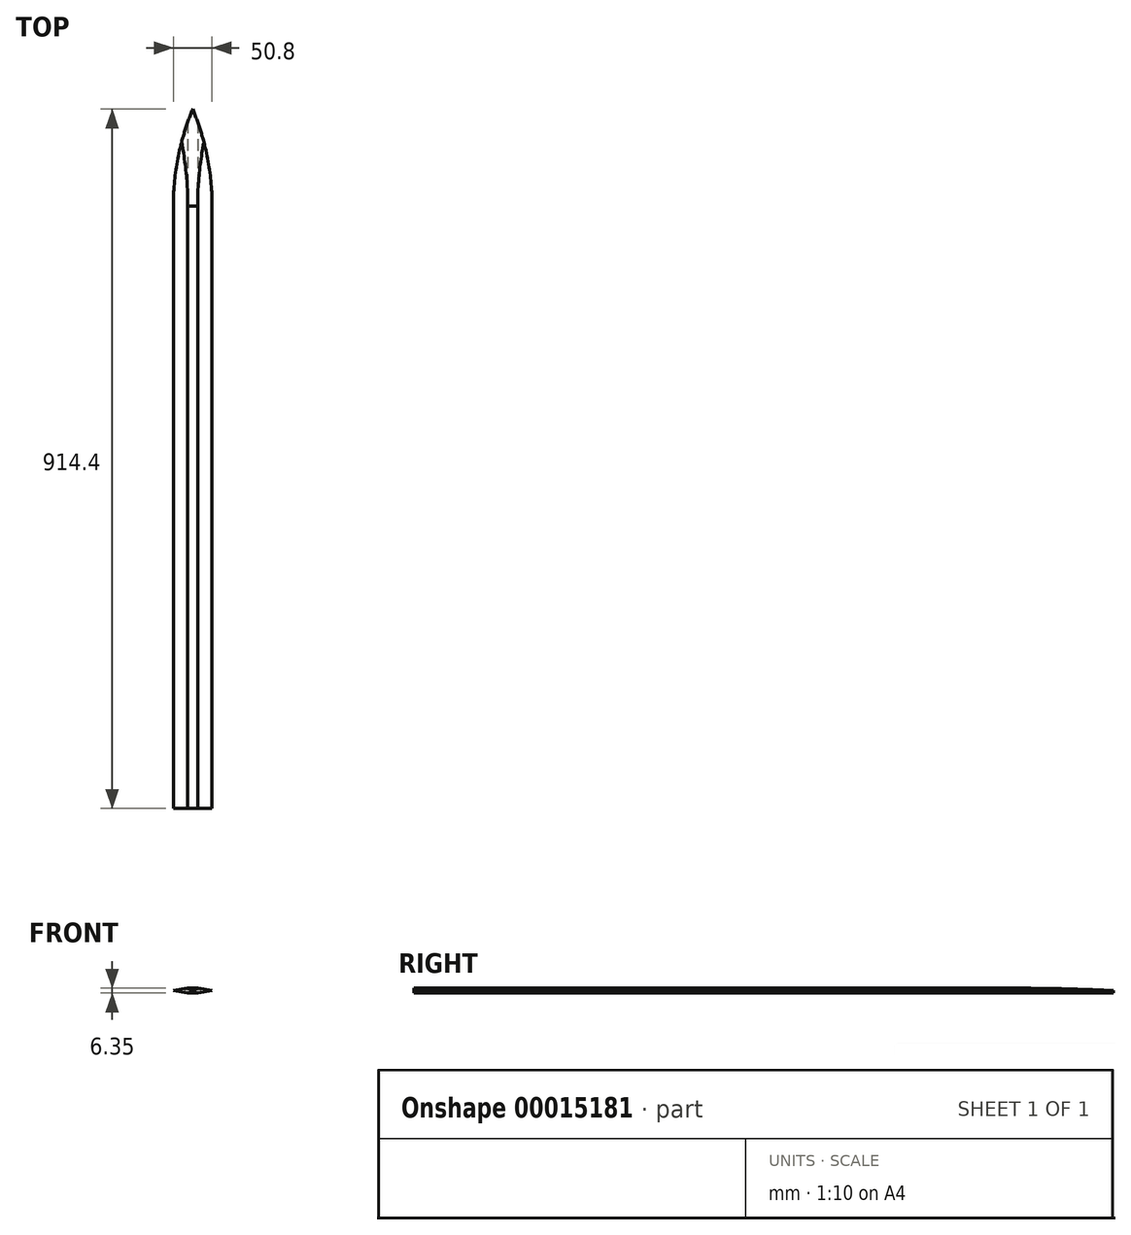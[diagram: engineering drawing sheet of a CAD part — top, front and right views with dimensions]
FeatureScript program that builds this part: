
annotation { "Feature Type Name" : "Feature", "Feature Type Description" : "" }
export const myFeature = defineFeature(function(context is Context, id is Id, definition is map)
    precondition{}
    {
        {
            var Q0;
            Q0=qCreatedBy(makeId("Top.planeOp"),FACE);
            var sketch = newSketch(context, id + "F0", { "sketchPlane" : qUnion([Q0])});
            skLineSegment(sketch, "E0.bottom", {"start": v(-196.6, 454.87) * mm, "end": v(-145.8, 454.87) * mm});
            skLineSegment(sketch, "E0.top", {"start": v(-196.6, -459.53) * mm, "end": v(-145.8, -459.53) * mm});
            skLineSegment(sketch, "E0.left", {"start": v(-196.6, 454.87) * mm, "end": v(-196.6, -459.53) * mm});
            skLineSegment(sketch, "E0.right", {"start": v(-145.8, 454.87) * mm, "end": v(-145.8, -459.53) * mm});
            skSolve(sketch);
        }
        {
            var Q0;
            Q0=makeQuery(id+"F0.imprint","IMPRINT",FACE,{"disambiguationData":[TD([[makeQuery(id+"F0.imprint","IMPRINT",EDGE,{"derivedFrom":sQuery(id+"F0.wireOp",EDGE,"E0.bottom")}),-1.0]])]});
            extrude(context, id + "F1", {"entities" : qUnion([Q0]), "depth" : 6.35 * mm});
        }
        {
            var Q0;
            Q0=makeQuery(id+"F1.opExtrude","SWEPT_FACE",FACE,{"disambiguationData":[OSD([sQuery(id+"F0.wireOp",EDGE,"E0.top")])]});
            var sketch = newSketch(context, id + "F2", { "sketchPlane" : qUnion([Q0])});
            skLineSegment(sketch, "E1", {"start": v(-171.2, 6.35) * mm, "end": v(-171.2, 0) * mm, "construction": true});
            skLineSegment(sketch, "E2", {"start": v(-196.6, 3.18) * mm, "end": v(-145.8, 3.18) * mm, "construction": true});
            skLineSegment(sketch, "E3", {"start": v(-177.56, 6.35) * mm, "end": v(-177.56, 3.17) * mm, "construction": true});
            skLineSegment(sketch, "E4", {"start": v(-164.86, 6.35) * mm, "end": v(-164.86, 3.17) * mm, "construction": true});
            skLineSegment(sketch, "E5", {"start": v(-177.56, 3.17) * mm, "end": v(-177.56, 0) * mm, "construction": true});
            skLineSegment(sketch, "E6", {"start": v(-164.86, 3.17) * mm, "end": v(-164.86, 0) * mm, "construction": true});
            skLineSegment(sketch, "E7", {"start": v(-177.56, 4.76) * mm, "end": v(-164.86, 4.76) * mm, "construction": true});
            skLineSegment(sketch, "E8", {"start": v(-177.56, 1.59) * mm, "end": v(-164.86, 1.59) * mm, "construction": true});
            skArc(sketch, "E9", {"start": v(-177.56, 6.35) * mm, "mid": v(-171.2, 4.76) * mm, "end": v(-164.86, 6.35) * mm});
            skArc(sketch, "E10", {"start": v(-164.86, 0) * mm, "mid": v(-171.2, 1.59) * mm, "end": v(-177.56, 0) * mm});
            skLineSegment(sketch, "E11", {"start": v(-145.8, 3.18) * mm, "end": v(-164.86, 0) * mm});
            skLineSegment(sketch, "E12", {"start": v(-145.8, 3.18) * mm, "end": v(-164.86, 6.35) * mm});
            skLineSegment(sketch, "E13", {"start": v(-177.56, 6.35) * mm, "end": v(-196.6, 3.18) * mm});
            skLineSegment(sketch, "E14", {"start": v(-196.6, 3.18) * mm, "end": v(-177.56, 0) * mm});
            skSolve(sketch);
        }
        {
            var Q0;
            {var subQ2=sQuery(id+"F2.wireOp",EDGE,"E13");Q0=makeQuery(id+"F2.imprint","IMPRINT",FACE,{"disambiguationData":[TD([[makeQuery(id+"F2.imprint","IMPRINT",EDGE,{"derivedFrom":subQ2}),-1.0]])]});}
            var Q1;
            {var subQ2=sQuery(id+"F2.wireOp",EDGE,"E14");Q1=makeQuery(id+"F2.imprint","IMPRINT",FACE,{"disambiguationData":[TD([[makeQuery(id+"F2.imprint","IMPRINT",EDGE,{"derivedFrom":subQ2}),-1.0]])]});}
            var Q2;
            {var subQ1=sQuery(id+"F2.wireOp",EDGE,"E10");Q2=makeQuery(id+"F2.imprint","IMPRINT",FACE,{"disambiguationData":[TD([[makeQuery(id+"F2.imprint","IMPRINT",EDGE,{"derivedFrom":subQ1}),1.0]])]});}
            var Q3;
            {var subQ1=sQuery(id+"F2.wireOp",EDGE,"E9");Q3=makeQuery(id+"F2.imprint","IMPRINT",FACE,{"disambiguationData":[TD([[makeQuery(id+"F2.imprint","IMPRINT",EDGE,{"derivedFrom":subQ1}),1.0]])]});}
            var Q4;
            {var subQ2=sQuery(id+"F2.wireOp",EDGE,"E12");Q4=makeQuery(id+"F2.imprint","IMPRINT",FACE,{"disambiguationData":[TD([[makeQuery(id+"F2.imprint","IMPRINT",EDGE,{"derivedFrom":subQ2}),-1.0]])]});}
            var Q5;
            {var subQ2=sQuery(id+"F2.wireOp",EDGE,"E11");Q5=makeQuery(id+"F2.imprint","IMPRINT",FACE,{"disambiguationData":[TD([[makeQuery(id+"F2.imprint","IMPRINT",EDGE,{"derivedFrom":subQ2}),1.0]])]});}
            extrude(context, id + "F3", {"entities" : qUnion([Q0, Q1, Q2, Q3, Q4, Q5]), "operationType" : NewBodyOperationType.REMOVE, "oppositeDirection" : true, "depth" : 787.4 * mm});
        }
        {
            var Q0;
            Q0=makeQuery(id+"F1.opExtrude","CAP_FACE",FACE,{"disambiguationData":[OSD([sQuery(id+"F0.wireOp",EDGE,"E0.bottom"),sQuery(id+"F0.wireOp",EDGE,"E0.top"),sQuery(id+"F0.wireOp",EDGE,"E0.left"),sQuery(id+"F0.wireOp",EDGE,"E0.right")])],"isStart":true});
            var sketch = newSketch(context, id + "F4", { "sketchPlane" : qUnion([Q0])});
            skArc(sketch, "E15", {"start": v(-171.2, -454.87) * mm, "mid": v(-152.22, -392.62) * mm, "end": v(-145.8, -327.87) * mm});
            skArc(sketch, "E16", {"start": v(-196.6, -327.87) * mm, "mid": v(-190.2, -392.62) * mm, "end": v(-171.2, -454.87) * mm});
            skSolve(sketch);
        }
        {
            var Q0;
            Q0=makeQuery(id+"F1.opExtrude","SWEPT_FACE",FACE,{"disambiguationData":[OSD([sQuery(id+"F0.wireOp",EDGE,"E0.left")])]});
            var sketch = newSketch(context, id + "F5", { "sketchPlane" : qUnion([Q0])});
            skArc(sketch, "E17", {"start": v(-327.87, 6.35) * mm, "mid": v(-391.39, 5.56) * mm, "end": v(-454.87, 3.17) * mm});
            skArc(sketch, "E18", {"start": v(-454.87, 3.18) * mm, "mid": v(-391.39, 0.8) * mm, "end": v(-327.87, 0) * mm});
            skSolve(sketch);
        }
        {
            var Q0;
            Q0 = qSketchRegion(id + "F5", true);
            var Q1;
            {var subQ2=sQuery(id+"F5.wireOp",EDGE,"E17");Q1=makeQuery(id+"F5.imprint","IMPRINT",FACE,{"disambiguationData":[TD([[makeQuery(id+"F5.imprint","IMPRINT",EDGE,{"derivedFrom":subQ2}),-1.0]])]});}
            extrude(context, id + "F6", {"entities" : qUnion([Q0, Q1]), "operationType" : NewBodyOperationType.REMOVE, "oppositeDirection" : true, "depth" : 62.83 * mm});
        }
        {
            var Q0;
            {var subQ1=sQuery(id+"F4.wireOp",EDGE,"E15");Q0=makeQuery(id+"F4.imprint","IMPRINT",FACE,{"disambiguationData":[TD([[makeQuery(id+"F4.imprint","IMPRINT",EDGE,{"derivedFrom":subQ1}),-1.0]])]});}
            var Q1;
            {var subQ1=sQuery(id+"F4.wireOp",EDGE,"E16");Q1=makeQuery(id+"F4.imprint","IMPRINT",FACE,{"disambiguationData":[TD([[makeQuery(id+"F4.imprint","IMPRINT",EDGE,{"derivedFrom":subQ1}),-1.0]])]});}
            extrude(context, id + "F7", {"entities" : qUnion([Q0, Q1]), "operationType" : NewBodyOperationType.REMOVE, "oppositeDirection" : true, "depth" : 25.4 * mm});
        }
        {
            var Q0;
            Q0=makeQuery(id+"F3.boolean.opBoolean","COPY",FACE,{"derivedFrom":makeQuery(id+"F3.opExtrude","CAP_FACE",FACE,{"disambiguationData":[OSD([sQuery(id+"F0.wireOp",EDGE,"E0.top"),sQuery(id+"F0.wireOp",EDGE,"E0.right"),sQuery(id+"F2.wireOp",EDGE,"E11")])],"isStart":false})});
            var Q1;
            Q1=makeQuery(id+"F3.boolean.opBoolean","COPY",FACE,{"derivedFrom":makeQuery(id+"F3.opExtrude","CAP_FACE",FACE,{"disambiguationData":[OSD([sQuery(id+"F0.wireOp",EDGE,"E0.top"),sQuery(id+"F0.wireOp",EDGE,"E0.right"),sQuery(id+"F2.wireOp",EDGE,"E12")])],"isStart":false})});
            var Q2;
            Q2=makeQuery(id+"F3.boolean.opBoolean","COPY",FACE,{"derivedFrom":makeQuery(id+"F3.opExtrude","CAP_FACE",FACE,{"disambiguationData":[OSD([sQuery(id+"F0.wireOp",EDGE,"E0.top"),sQuery(id+"F0.wireOp",EDGE,"E0.left"),sQuery(id+"F2.wireOp",EDGE,"E14")])],"isStart":false})});
            var Q3;
            Q3=makeQuery(id+"F3.boolean.opBoolean","COPY",FACE,{"derivedFrom":makeQuery(id+"F3.opExtrude","CAP_FACE",FACE,{"disambiguationData":[OSD([sQuery(id+"F0.wireOp",EDGE,"E0.top"),sQuery(id+"F0.wireOp",EDGE,"E0.left"),sQuery(id+"F2.wireOp",EDGE,"E13")])],"isStart":false})});
            extrude(context, id + "F8", {"entities" : qUnion([Q0, Q1, Q2, Q3]), "operationType" : NewBodyOperationType.REMOVE, "oppositeDirection" : true, "depth" : 161.17 * mm});
        }
        {
            var Q0;
            Q0=makeQuery(id+"F1.opExtrude","SWEPT_FACE",FACE,{"disambiguationData":[OSD([sQuery(id+"F0.wireOp",EDGE,"E0.top")])]});
            var sketch = newSketch(context, id + "F9", { "sketchPlane" : qUnion([Q0])});
            skLineSegment(sketch, "E19.bottom", {"start": v(-177.56, 6.35) * mm, "end": v(-177.56, 6.35) * mm});
            skLineSegment(sketch, "E19.top", {"start": v(-177.56, 0) * mm, "end": v(-177.56, 0) * mm});
            skLineSegment(sketch, "E19.left", {"start": v(-177.56, 6.35) * mm, "end": v(-177.56, 0) * mm});
            skLineSegment(sketch, "E19.right", {"start": v(-177.56, 6.35) * mm, "end": v(-177.56, 0) * mm});
            skLineSegment(sketch, "E20.bottom", {"start": v(-164.86, 0) * mm, "end": v(-164.86, 0) * mm});
            skLineSegment(sketch, "E20.top", {"start": v(-164.86, 6.35) * mm, "end": v(-164.86, 6.35) * mm});
            skLineSegment(sketch, "E20.left", {"start": v(-164.86, 0) * mm, "end": v(-164.86, 6.35) * mm});
            skLineSegment(sketch, "E20.right", {"start": v(-164.86, 0) * mm, "end": v(-164.86, 6.35) * mm});
            skLineSegment(sketch, "E21", {"start": v(-177.56, 6.35) * mm, "end": v(-164.86, 6.35) * mm});
            skLineSegment(sketch, "E22", {"start": v(-164.86, 0) * mm, "end": v(-177.56, 0) * mm});
            skSolve(sketch);
        }
        {
            var Q0;
            Q0=makeQuery(id+"F9.imprint","IMPRINT",FACE,{"disambiguationData":[TD([[makeQuery(id+"F9.imprint","IMPRINT",EDGE,{"derivedFrom":sQuery(id+"F9.wireOp",EDGE,"E22")}),-1.0]])]});
            var Q1;
            Q1=makeQuery(id+"F9.imprint","IMPRINT",FACE,{"disambiguationData":[TD([[makeQuery(id+"F9.imprint","IMPRINT",EDGE,{"derivedFrom":sQuery(id+"F9.wireOp",EDGE,"E19.right")}),1.0]])]});
            var Q2;
            Q2=makeQuery(id+"F9.imprint","IMPRINT",FACE,{"disambiguationData":[TD([[makeQuery(id+"F9.imprint","IMPRINT",EDGE,{"derivedFrom":sQuery(id+"F9.wireOp",EDGE,"E21")}),-1.0]])]});
            extrude(context, id + "F10", {"entities" : qUnion([Q0, Q1, Q2]), "operationType" : NewBodyOperationType.ADD, "depth" : 127 * mm});
        }
        {
            var Q0;
            Q0=makeQuery(id+"F10.opExtrude","SWEPT_FACE",FACE,{"disambiguationData":[OSD([sQuery(id+"F9.wireOp",EDGE,"E21")])]});
            extrude(context, id + "F11", {"entities" : qUnion([Q0]), "operationType" : NewBodyOperationType.REMOVE, "oppositeDirection" : true, "depth" : 1.78 * mm});
        }
        {
            var Q0;
            Q0=makeQuery(id+"F10.opExtrude","SWEPT_FACE",FACE,{"disambiguationData":[OSD([sQuery(id+"F9.wireOp",EDGE,"E22")])]});
            extrude(context, id + "F12", {"entities" : qUnion([Q0]), "operationType" : NewBodyOperationType.REMOVE, "oppositeDirection" : true, "depth" : 1.78 * mm});
        }
    });
